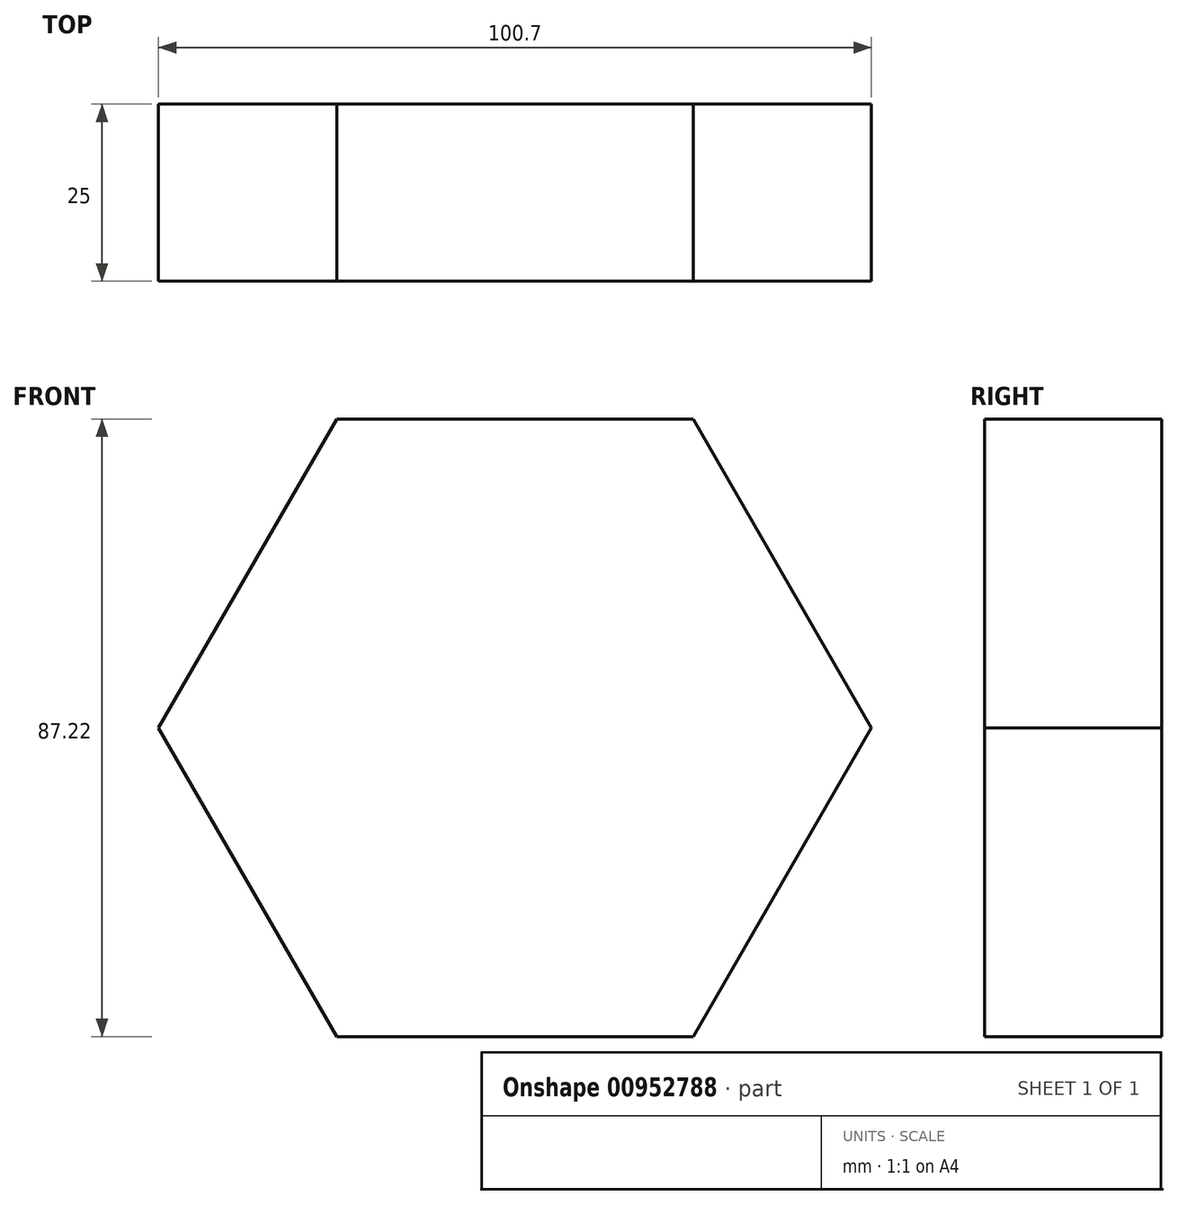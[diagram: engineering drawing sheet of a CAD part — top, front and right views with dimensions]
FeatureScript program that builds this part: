
annotation { "Feature Type Name" : "Feature", "Feature Type Description" : "" }
export const myFeature = defineFeature(function(context is Context, id is Id, definition is map)
    precondition{}
    {
        {
            var Q0;
            Q0=qCreatedBy(makeId("Front.planeOp"),FACE);
            var sketch = newSketch(context, id + "F0", { "sketchPlane" : qUnion([Q0])});
            skCircle(sketch, "E0.cCircle", {"center": v(0, 0) * mm, "radius": 43.6 * mm, "construction": true});
            skLineSegment(sketch, "E0.0", {"start": v(-25.18, 43.6) * mm, "end": v(25.18, 43.6) * mm});
            skLineSegment(sketch, "E0.1", {"start": v(25.18, 43.6) * mm, "end": v(50.35, 0) * mm});
            skLineSegment(sketch, "E0.2", {"start": v(50.35, 0) * mm, "end": v(25.18, -43.6) * mm});
            skLineSegment(sketch, "E0.3", {"start": v(25.18, -43.6) * mm, "end": v(-25.18, -43.6) * mm});
            skLineSegment(sketch, "E0.4", {"start": v(-25.18, -43.6) * mm, "end": v(-50.35, 0) * mm});
            skLineSegment(sketch, "E0.5", {"start": v(-50.35, 0) * mm, "end": v(-25.18, 43.6) * mm});
            skPoint(sketch, "E0.0.midPoint", {"position": v(0, 43.6) * mm});
            skSolve(sketch);
        }
        {
            var Q0;
            Q0 = qSketchRegion(id + "F0", true);
            extrude(context, id + "F1", {"entities" : qUnion([Q0]), "depth" : 25 * mm, "offsetDistance" : 25 * mm});
        }
    });
